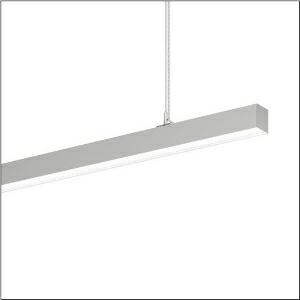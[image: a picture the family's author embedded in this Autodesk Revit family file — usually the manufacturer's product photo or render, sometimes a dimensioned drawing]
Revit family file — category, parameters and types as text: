
# Revit family: silica_r__21_51mx30db35sb_46d1
name_source: partatom
category: Lighting Fixtures
units: mm (PartAtom-declared; Revit-internal decimal feet)

## family parameters
Cut with Voids When Loaded = No
Host = Face
Light Source = No
Part Type = Normal
Room Calculation Point = No
Round Connector Dimension = Use Diameter
Shared = No

## types (1)
- --- (1 x LED, 5260 lm, 34.1 W, 3000K)
    Apparent Load = 34 VA
    CIE Flux Codes = 47 79 96 57 100
    Color Rendering = 80
    Color Temperature = 3000K
    Default Elevation = 1800 mm
    Description = Silica® 21, office luminaire, primary optical cover: cover, of PMMA, opal, light emission: direct/indirect distribution, primary light characteristic: symmetric, installation type: suspended mounting, LED, rated luminous flux: 5.260lm, luminous efficacy: 154lm/W, light colour: 830, colour temperature: 3000K, control gear: DALI 2, with terminal, 3+2-pole, max. 2.5mm², mains connection: 220..240V, AC, 50/60Hz, rated input power: 34.1W, luminaire housing, of aluminium, metallic grey (RAL 9006), length: 1.504mm, width: 53mm, height: 53mm, protection rating (complete): IP20, insulation class (complete): insulation class I (protective earthing), certification: CE, permissible operating ambient temperature: 0..+35°C, standard: EN 50419, packaging unit: 1 piece
    Height = 53 mm
    Lamp = 1 x LED
    Lamp Light Flux = 5260 lm
    Lamp Power = 34.1 W
    Lamp count = 1
    Length = 1504 mm
    Luminous efficacy = 154 lm/W
    Manufacturer = Siteco
    ModVariant = No
    Model = 51MX30DB35SB
    Mounting Place = Ceiling
    Mounting Type = Pendant
    Number of Poles = 1
    OnlyDefault = Yes
    Power Factor = 1
    Product Name = Silica® 21
    Product group = office luminaire | ceiling pendant
    ProductGroupID = 904
    Protection Class = Protection class I
    Protection Degree = IP 20
    RLX_Detail_Level = 1
    RLX_Emergency_Light_Flux = 0 lm
    RLX_Emergency_Type = 0
    RLX_Emergency_Type_DB = No
    RlxData = <blob elided: 23413 chars, md5=60175342>
    Socket = socket
    Standby Power = 0 W
    System Light Flux = 5260 lm
    System Power = 34 W
    Type Comments = factory setting: luminous flux: 100 % | dim-lin: 254 | 233 mA
    Type Image = l_1335864.jpg
    URL = http://relux.com
    VarID = @adj_116894
    Voltage = 0 V
    Weight = 0.00 kg
    Width = 53 mm

## geometry (parser evidence)
native form markers: Blend x4, Sweep x13
no freeform markers — native parametric forms only
